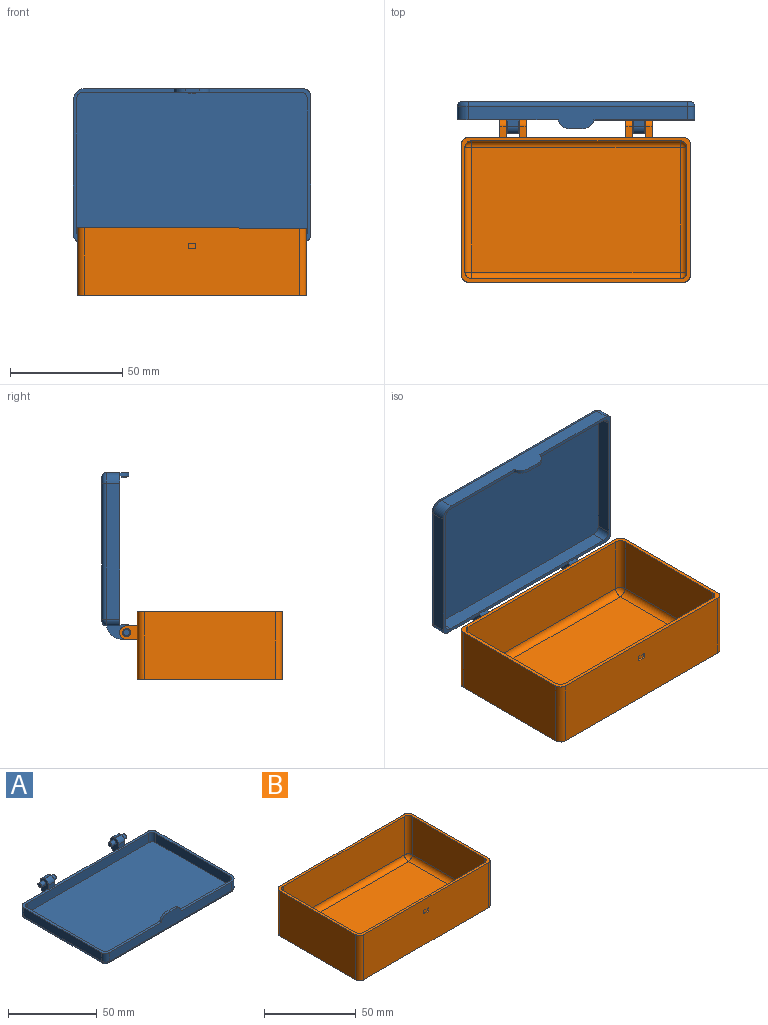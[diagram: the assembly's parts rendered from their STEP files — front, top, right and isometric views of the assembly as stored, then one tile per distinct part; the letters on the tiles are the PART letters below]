
ASSEMBLY  parts=2 mates=1
PART A: 158 faces, bbox 761.3x75.2x14.2 mm
  f0: plane 19.3x6mm, normal (0,1,0), area 115.8mm2, adj f1,f11,f28,f132
  f1: plane 105.8x68.3mm, normal (0,0,1), area 480.9mm2, adj f0,f2,f4,f5,f6,f7,f8,f9
  f2: plane 51.2x6mm, normal (0,1,0), area 307.2mm2, adj f1,f28,f128,f134
  f3: plane 101.8x64.3mm, normal (0,0,-1), area 6346.7mm2, adj f21,f22,f23,f24,f25,f26,f27,f28
  f4: plane 19.3x6mm, normal (0,1,0), area 115.8mm2, adj f1,f5,f28,f126
  f5: cylinder r=3mm len=6mm, axis (0,0,1), area 28.3mm2, adj f1,f4,f6,f27
  f6: plane 62.3x6mm, normal (-1,0,0), area 373.8mm2, adj f1,f5,f7,f25
  f7: cylinder r=3mm len=6mm, axis (0,0,1), area 28.3mm2, adj f1,f6,f8,f23
  f8: plane 97.8x10mm, normal (0,-1,0), area 640.9mm2, adj f1,f7,f9,f21,f150,f151,f152
  f9: cylinder r=5mm len=6mm, axis (0,0,1), area 47.1mm2, adj f1,f8,f10,f22
  f10: plane 60.3x6mm, normal (1,0,0), area 361.8mm2, adj f1,f9,f11,f24
  f11: cylinder r=3mm len=6mm, axis (0,0,1), area 28.3mm2, adj f0,f1,f10,f26
  f12: plane 59.3x6.5mm, normal (-1,0,0), area 385.4mm2, adj f1,f13,f19,f20
  f13: cylinder r=3mm len=6.5mm, axis (0,0,1), area 30.6mm2, adj f1,f12,f14,f20
  f14: plane 96.8x6.5mm, normal (0,-1,0), area 629.2mm2, adj f1,f13,f15,f20
  f15: cylinder r=3mm len=6.5mm, axis (0,0,1), area 30.6mm2, adj f1,f14,f16,f20
  f16: plane 59.3x6.5mm, normal (1,0,0), area 385.4mm2, adj f1,f15,f17,f20
  f17: cylinder r=3mm len=6.5mm, axis (0,0,1), area 30.6mm2, adj f1,f16,f18,f20
  f18: plane 96.8x10.5mm, normal (0,1,0), area 677.3mm2, adj f1,f17,f19,f20,f150,f151,f152,f153
  f19: cylinder r=3mm len=6.5mm, axis (0,0,1), area 30.6mm2, adj f1,f12,f18,f20
  f20: plane 102.8x65.3mm, normal (0,0,1), area 6705.1mm2, adj f12,f13,f14,f15,f16,f17,f18,f19
  f21: cylinder r=2mm len=97.8mm, axis (-1,0,0), area 307.2mm2, adj f3,f8,f22,f23
  f22: torus R=3mm, axis (0,0,1), area 21.1mm2, adj f3,f9,f21,f24
  f23: torus R=1mm, axis (0,0,1), area 11.2mm2, adj f3,f7,f21,f25
  f24: cylinder r=2mm len=60.3mm, axis (0,-1,0), area 189.4mm2, adj f3,f10,f22,f26
  f25: cylinder r=2mm len=62.3mm, axis (0,1,0), area 195.7mm2, adj f3,f6,f23,f27
  f26: torus R=1mm, axis (0,0,1), area 11.2mm2, adj f3,f11,f24,f28
  f27: torus R=1mm, axis (0,0,1), area 11.2mm2, adj f3,f5,f25,f28
  f28: cylinder r=2mm len=99.8mm, axis (1,0,0), area 313.5mm2, adj f0,f2,f3,f4,f26,f27,f148,f149
  f29: plane 2.99x0.5mm, normal (1,0,0), area 1.5mm2, adj f3,f30,f47,f48
  f30: plane 0.88x0.5mm, normal (0,1,0), area 0.4mm2, adj f3,f29,f31,f48
  f31: plane 2.99x1.86mm, normal (-0.85,0.53,0), area 1.8mm2, adj f3,f30,f32,f48
  f32: plane 1.83x0.5mm, normal (0,1,0), area 0.9mm2, adj f3,f31,f33,f48
  f33: extruded ~3.4x2.29mm, area 2mm2, adj f3,f32,f34,f48
  f34: extruded ~1.07x0.84mm, area 0.7mm2, adj f3,f33,f35,f48
  f35: extruded ~1.22x0.5mm, area 0.7mm2, adj f3,f34,f36,f48
  f36: extruded ~1.76x0.76mm, area 1mm2, adj f3,f35,f37,f48
  f37: extruded ~2.35x0.58mm, area 1.2mm2, adj f3,f36,f38,f48
  f38: plane 2.27x0.5mm, normal (0,-1,0), area 1.1mm2, adj f3,f37,f39,f48
  f39: plane 7.79x0.5mm, normal (-1,0,0), area 3.9mm2, adj f3,f38,f47,f48
  f40: plane 0.53x0.5mm, normal (0,-1,0), area 0.3mm2, adj f41,f46,f48,f49
  f41: plane 2.1x0.5mm, normal (1,0,0), area 1.1mm2, adj f40,f42,f48,f49
  f42: plane 0.5x0.5mm, normal (0,1,0), area 0.3mm2, adj f41,f43,f48,f49
  f43: extruded ~1.18x0.5mm, area 0.6mm2, adj f42,f44,f48,f49
  f44: extruded ~0.79x0.5mm, area 0.5mm2, adj f43,f45,f48,f49
  f45: extruded ~0.82x0.5mm, area 0.5mm2, adj f44,f46,f48,f49
  f46: extruded ~1.16x0.5mm, area 0.6mm2, adj f40,f45,f48,f49
  f47: plane 1.65x0.5mm, normal (0,1,0), area 0.8mm2, adj f3,f29,f39,f48
  f48: plane 7.79x6.22mm, normal (0,0,-1), area 29.6mm2, adj f29,f30,f31,f32,f33,f34,f35,f36
  f49: plane 2.1x2.06mm, normal (0,0,-1), area 3.8mm2, adj f40,f41,f42,f43,f44,f45,f46
  f50: extruded ~2.85x0.88mm, area 1.5mm2, adj f51,f61,f62,f125
  f51: plane 2.03x0.5mm, normal (0,-1,0), area 1mm2, adj f50,f52,f62,f125
  f52: extruded ~3.37x1.01mm, area 1.8mm2, adj f51,f61,f62,f125
  f53: plane 1.86x0.56mm, normal (-0.96,0.29,0), area 1mm2, adj f3,f54,f60,f62
  f54: plane 1.78x0.5mm, normal (0,1,0), area 0.9mm2, adj f3,f53,f55,f62
  f55: plane 7.82x2.76mm, normal (0.94,-0.33,0), area 4.1mm2, adj f3,f54,f56,f62
  f56: plane 2.02x0.5mm, normal (0,-1,0), area 1mm2, adj f3,f55,f57,f62
  f57: plane 7.82x2.75mm, normal (-0.94,-0.33,0), area 4.1mm2, adj f3,f56,f58,f62
  f58: plane 1.78x0.5mm, normal (0,1,0), area 0.9mm2, adj f3,f57,f59,f62
  f59: plane 1.86x0.56mm, normal (0.96,0.29,0), area 1mm2, adj f3,f58,f60,f62
  f60: plane 2.84x0.5mm, normal (0,1,0), area 1.4mm2, adj f3,f53,f59,f62
  f61: extruded ~0.52x0.5mm, area 0.3mm2, adj f50,f52,f62,f125
  f62: plane 7.82x7.53mm, normal (0,0,-1), area 27.7mm2, adj f50,f51,f52,f53,f54,f55,f56,f57
  f63: plane 4.49x0.5mm, normal (0,1,0), area 2.2mm2, adj f3,f64,f74,f75
  f64: plane 1.36x0.5mm, normal (1,0,0), area 0.7mm2, adj f3,f63,f65,f75
  f65: plane 2.83x0.5mm, normal (0,-1,0), area 1.4mm2, adj f3,f64,f66,f75
  f66: plane 2.01x0.5mm, normal (1,0,0), area 1mm2, adj f3,f65,f67,f75
  f67: plane 2.64x0.5mm, normal (0,1,0), area 1.3mm2, adj f3,f66,f68,f75
  f68: plane 1.35x0.5mm, normal (1,0,0), area 0.7mm2, adj f3,f67,f69,f75
  f69: plane 2.64x0.5mm, normal (0,-1,0), area 1.3mm2, adj f3,f68,f70,f75
  f70: plane 1.71x0.5mm, normal (1,0,0), area 0.9mm2, adj f3,f69,f71,f75
  f71: plane 2.83x0.5mm, normal (0,1,0), area 1.4mm2, adj f3,f70,f72,f75
  f72: plane 1.35x0.5mm, normal (1,0,0), area 0.7mm2, adj f3,f71,f73,f75
  f73: plane 4.49x0.5mm, normal (0,-1,0), area 2.2mm2, adj f3,f72,f74,f75
  f74: plane 7.79x0.5mm, normal (-1,0,0), area 3.9mm2, adj f3,f63,f73,f75
  f75: plane 7.79x4.49mm, normal (0,0,-1), area 24.1mm2, adj f63,f64,f65,f66,f67,f68,f69,f70
  f76: plane 2.1x0.5mm, normal (0,1,0), area 1mm2, adj f3,f77,f89,f90
  f77: plane 7.79x0.5mm, normal (1,0,0), area 3.9mm2, adj f3,f76,f78,f90
  f78: plane 1.49x0.5mm, normal (0,-1,0), area 0.7mm2, adj f3,f77,f79,f90
  f79: plane 3.69x0.5mm, normal (-1,0,0), area 1.8mm2, adj f3,f78,f80,f90
  f80: extruded ~2.15x0.5mm, area 1.1mm2, adj f3,f79,f81,f90
  f81: plane 0.5x0.04mm, normal (0,-1,0), area 0mm2, adj f3,f80,f82,f90
  f82: plane 5.84x3.38mm, normal (0.87,-0.5,0), area 3.4mm2, adj f3,f81,f83,f90
  f83: plane 2.08x0.5mm, normal (0,-1,0), area 1mm2, adj f3,f82,f84,f90
  f84: plane 7.79x0.5mm, normal (-1,0,0), area 3.9mm2, adj f3,f83,f85,f90
  f85: plane 1.48x0.5mm, normal (0,1,0), area 0.7mm2, adj f3,f84,f86,f90
  f86: plane 3.67x0.5mm, normal (1,0,0), area 1.8mm2, adj f3,f85,f87,f90
  f87: extruded ~2.23x0.5mm, area 1.1mm2, adj f3,f86,f88,f90
  f88: plane 0.5x0.05mm, normal (0,1,0), area 0mm2, adj f3,f87,f89,f90
  f89: plane 5.89x3.39mm, normal (-0.87,0.5,0), area 3.4mm2, adj f3,f76,f88,f90
  f90: plane 7.79x6.91mm, normal (0,0,-1), area 34.4mm2, adj f76,f77,f78,f79,f80,f81,f82,f83
  f91: plane 7.79x0.5mm, normal (-1,0,0), area 3.9mm2, adj f3,f92,f94,f95
  f92: plane 1.65x0.5mm, normal (0,1,0), area 0.8mm2, adj f3,f91,f93,f95
  f93: plane 7.79x0.5mm, normal (1,0,0), area 3.9mm2, adj f3,f92,f94,f95
  f94: plane 1.65x0.5mm, normal (0,-1,0), area 0.8mm2, adj f3,f91,f93,f95
  f95: plane 7.79x1.65mm, normal (0,0,-1), area 12.9mm2, adj f91,f92,f93,f94
  f96: plane 1.65x0.5mm, normal (0,1,0), area 0.8mm2, adj f3,f97,f103,f104
  f97: plane 6.42x0.5mm, normal (1,0,0), area 3.2mm2, adj f3,f96,f98,f104
  f98: plane 2.11x0.5mm, normal (0,1,0), area 1.1mm2, adj f3,f97,f99,f104
  f99: plane 1.37x0.5mm, normal (1,0,0), area 0.7mm2, adj f3,f98,f100,f104
  f100: plane 5.88x0.5mm, normal (0,-1,0), area 2.9mm2, adj f3,f99,f101,f104
  f101: plane 1.37x0.5mm, normal (-1,0,0), area 0.7mm2, adj f3,f100,f102,f104
  f102: plane 2.12x0.5mm, normal (0,1,0), area 1.1mm2, adj f3,f101,f103,f104
  f103: plane 6.42x0.5mm, normal (-1,0,0), area 3.2mm2, adj f3,f96,f102,f104
  f104: plane 7.79x5.88mm, normal (0,0,-1), area 18.7mm2, adj f96,f97,f98,f99,f100,f101,f102,f103
  f105: plane 6.11x1.88mm, normal (-0.96,0.29,0), area 3.2mm2, adj f3,f106,f123,f124
  f106: plane 1.51x0.5mm, normal (0,1,0), area 0.8mm2, adj f3,f105,f107,f124
  f107: plane 6.1x2.01mm, normal (0.95,0.31,0), area 3.2mm2, adj f3,f106,f108,f124
  f108: plane 0.5x0.05mm, normal (0,1,0), area 0mm2, adj f3,f107,f109,f124
  f109: extruded ~1.81x0.5mm, area 0.9mm2, adj f3,f108,f110,f124
  f110: extruded ~0.6x0.5mm, area 0.3mm2, adj f3,f109,f111,f124
  f111: plane 3.69x0.5mm, normal (-1,0,0), area 1.8mm2, adj f3,f110,f112,f124
  f112: plane 1.54x0.5mm, normal (0,1,0), area 0.8mm2, adj f3,f111,f113,f124
  f113: plane 7.79x0.5mm, normal (1,0,0), area 3.9mm2, adj f3,f112,f114,f124
  f114: plane 2.25x0.5mm, normal (0,-1,0), area 1.1mm2, adj f3,f113,f115,f124
  f115: plane 5.96x1.96mm, normal (-0.95,-0.31,0), area 3.1mm2, adj f3,f114,f116,f124
  f116: plane 0.5x0.03mm, normal (0,-1,0), area 0mm2, adj f3,f115,f117,f124
  f117: plane 5.96x1.84mm, normal (0.96,-0.3,0), area 3.1mm2, adj f3,f116,f118,f124
  f118: plane 2.25x0.5mm, normal (0,-1,0), area 1.1mm2, adj f3,f117,f119,f124
  f119: plane 7.79x0.5mm, normal (-1,0,0), area 3.9mm2, adj f3,f118,f120,f124
  f120: plane 1.48x0.5mm, normal (0,1,0), area 0.7mm2, adj f3,f119,f121,f124
  f121: plane 3.62x0.5mm, normal (1,0,0), area 1.8mm2, adj f3,f120,f122,f124
  f122: extruded ~2.49x0.5mm, area 1.2mm2, adj f3,f121,f123,f124
  f123: plane 0.5x0.05mm, normal (0,1,0), area 0mm2, adj f3,f105,f122,f124
  f124: plane 8.33x7.79mm, normal (0,0,-1), area 41.9mm2, adj f105,f106,f107,f108,f109,f110,f111,f112
  f125: plane 3.37x2.03mm, normal (0,0,-1), area 3.4mm2, adj f50,f51,f52,f61
  f126: plane 12.18x6.68mm, normal (-1,0,0), area 54.9mm2, adj f1,f4,f127,f129,f130,f138,f139,f140
  f127: plane 5x3mm, normal (0,-1,0), area 15mm2, adj f1,f126,f128,f139
  f128: plane 12.18x6.67mm, normal (1,0,0), area 54.8mm2, adj f1,f2,f127,f129,f130,f138,f139,f142
  f129: plane 5x2.07mm, normal (0,1,0), area 10.4mm2, adj f126,f128,f138,f149
  f130: plane 5x0.5mm, normal (0,0,1), area 2.5mm2, adj f126,f128,f138,f139
  f131: plane 5x3mm, normal (0,-1,0), area 15mm2, adj f1,f132,f134,f137
  f132: plane 12x6.5mm, normal (1,0,0), area 54.9mm2, adj f0,f1,f131,f133,f135,f136,f137,f144
  f133: plane 5x2.07mm, normal (0,1,0), area 10.4mm2, adj f132,f134,f136,f148
  f134: plane 12x6.5mm, normal (-1,0,0), area 54.9mm2, adj f1,f2,f131,f133,f135,f136,f137,f146
  f135: plane 5x0.5mm, normal (0,0,1), area 2.5mm2, adj f132,f134,f136,f137
  f136: cylinder r=3mm len=5mm, axis (1,0,0), area 23.6mm2, adj f132,f133,f134,f135
  f137: cylinder r=3mm len=5mm, axis (-1,0,0), area 23.6mm2, adj f131,f132,f134,f135
  f138: cylinder r=3mm len=5.01mm, axis (1,0,0), area 23.6mm2, adj f126,f128,f129,f130
  f139: cylinder r=3mm len=5mm, axis (-1,0,0), area 23.6mm2, adj f126,f127,f128,f130
  f140: cylinder r=1.4mm len=3.4mm, axis (1,0,0), area 29.9mm2, adj f126,f141
  f141: plane 2.8x2.8mm, normal (-1,0,0), area 6.2mm2, adj f140
  f142: cylinder r=1.4mm len=3.4mm, axis (-1,0,0), area 29.9mm2, adj f128,f143
  f143: plane 2.8x2.8mm, normal (1,0,0), area 6.2mm2, adj f142
  f144: cylinder r=1.4mm len=3.4mm, axis (-1,0,0), area 29.9mm2, adj f132,f145
  f145: plane 2.8x2.8mm, normal (1,0,0), area 6.2mm2, adj f144
  f146: cylinder r=1.4mm len=3.4mm, axis (1,0,0), area 29.9mm2, adj f134,f147
  f147: plane 2.8x2.8mm, normal (-1,0,0), area 6.2mm2, adj f146
  f148: cylinder r=7mm len=6.93mm, axis (1,0,0), area 50mm2, adj f28,f132,f133,f134
  f149: bspline ~761.14x6.97mm, area 50mm2, adj f28,f126,f128,f129
  f150: plane 6.2x1.5mm, normal (0,0,1), area 9.3mm2, adj f8,f18,f151,f152
  f151: cylinder r=5mm len=4.9mm, axis (0,1,0), area 10.3mm2, adj f1,f8,f18,f150
  f152: cylinder r=5mm len=4.9mm, axis (0,1,0), area 10.3mm2, adj f1,f8,f18,f150
  f153: plane 2x0.8mm, normal (-1,0,0), area 1.6mm2, adj f18,f154,f156,f157
  f154: plane 3x0.8mm, normal (0,0,1), area 2.4mm2, adj f18,f153,f155,f157
  f155: plane 2x0.8mm, normal (1,0,0), area 1.6mm2, adj f18,f154,f156,f157
  f156: plane 3x0.8mm, normal (0,0,-1), area 2.4mm2, adj f18,f153,f155,f157
  f157: plane 3x2mm, normal (0,1,0), area 6mm2, adj f153,f154,f155,f156
PART B: 56 faces, bbox 102x72.5x30 mm
  f0: plane 96x30mm, normal (0,-1,0), area 2871.8mm2, adj f2,f5,f6,f9,f39,f40,f41,f42
  f1: plane 96x30mm, normal (0,1,0), area 2808mm2, adj f2,f3,f8,f9,f15,f16,f17,f18
  f2: plane 102x64.5mm, normal (0,0,1), area 490.5mm2, adj f0,f1,f3,f4,f5,f6,f7,f8
  f3: cylinder r=3mm len=30mm, axis (0,0,1), area 141.4mm2, adj f1,f2,f4,f9
  f4: plane 58.5x30mm, normal (-1,0,0), area 1755mm2, adj f2,f3,f5,f9
  f5: cylinder r=3mm len=30mm, axis (0,0,1), area 141.4mm2, adj f0,f2,f4,f9
  f6: cylinder r=3mm len=30mm, axis (0,0,1), area 141.4mm2, adj f0,f2,f7,f9
  f7: plane 58.5x30mm, normal (1,0,0), area 1755mm2, adj f2,f6,f8,f9
  f8: cylinder r=3mm len=30mm, axis (0,0,1), area 141.4mm2, adj f1,f2,f7,f9
  f9: plane 102x64.5mm, normal (0,0,-1), area 6571.3mm2, adj f0,f1,f3,f4,f5,f6,f7,f8
  f10: plane 93x25.5mm, normal (0,1,0), area 2371.5mm2, adj f2,f49,f52,f55
  f11: plane 93x55.5mm, normal (0,0,1), area 5161.5mm2, adj f45,f50,f51,f55
  f12: plane 93x25.5mm, normal (0,-1,0), area 2371.5mm2, adj f2,f44,f45,f46
  f13: plane 55.5x25.5mm, normal (1,0,0), area 1415.3mm2, adj f2,f44,f49,f50
  f14: plane 55.5x25.5mm, normal (-1,0,0), area 1415.3mm2, adj f2,f46,f51,f52
  f15: plane 8x6mm, normal (-1,0,0), area 34mm2, adj f1,f17,f18,f34,f38
  f16: plane 8x6mm, normal (1,0,0), area 34mm2, adj f1,f17,f18,f34,f38
  f17: plane 5x3mm, normal (0,0,-1), area 15mm2, adj f1,f15,f16,f38
  f18: plane 5x3mm, normal (0,0,1), area 15mm2, adj f1,f15,f16,f38
  f19: plane 8x6mm, normal (-1,0,0), area 34mm2, adj f1,f21,f22,f33,f37
  f20: plane 8x6mm, normal (1,0,0), area 34mm2, adj f1,f21,f22,f33,f37
  f21: plane 5x3mm, normal (0,0,-1), area 15mm2, adj f1,f19,f20,f37
  f22: plane 5x3mm, normal (0,0,1), area 15mm2, adj f1,f19,f20,f37
  f23: plane 8x6mm, normal (-1,0,0), area 34mm2, adj f1,f25,f26,f32,f36
  f24: plane 8x6mm, normal (1,0,0), area 34mm2, adj f1,f25,f26,f32,f36
  f25: plane 5x3mm, normal (0,0,-1), area 15mm2, adj f1,f23,f24,f36
  f26: plane 5x3mm, normal (0,0,1), area 15mm2, adj f1,f23,f24,f36
  f27: plane 8x6mm, normal (-1,0,0), area 34mm2, adj f1,f29,f30,f31,f35
  f28: plane 8x6mm, normal (1,0,0), area 34mm2, adj f1,f29,f30,f31,f35
  f29: plane 5x3mm, normal (0,0,-1), area 15mm2, adj f1,f27,f28,f35
  f30: plane 5x3mm, normal (0,0,1), area 15mm2, adj f1,f27,f28,f35
  f31: cylinder r=1.8mm len=3.6mm, axis (1,0,0), area 33.9mm2, adj f27,f28
  f32: cylinder r=1.8mm len=3.6mm, axis (1,0,0), area 33.9mm2, adj f23,f24
  f33: cylinder r=1.8mm len=3.6mm, axis (1,0,0), area 33.9mm2, adj f19,f20
  f34: cylinder r=1.8mm len=3.6mm, axis (1,0,0), area 33.9mm2, adj f15,f16
  f35: cylinder r=3mm len=6mm, axis (1,0,0), area 28.3mm2, adj f27,f28,f29,f30
  f36: cylinder r=3mm len=6mm, axis (1,0,0), area 28.3mm2, adj f23,f24,f25,f26
  f37: cylinder r=3mm len=6mm, axis (1,0,0), area 28.3mm2, adj f19,f20,f21,f22
  f38: cylinder r=3mm len=6mm, axis (1,0,0), area 28.3mm2, adj f15,f16,f17,f18
  f39: plane 3.4x0.75mm, normal (0,0,1), area 2.6mm2, adj f0,f40,f42,f43
  f40: plane 2.4x0.75mm, normal (-1,0,0), area 1.8mm2, adj f0,f39,f41,f43
  f41: plane 3.4x0.75mm, normal (0,0,-1), area 2.6mm2, adj f0,f40,f42,f43
  f42: plane 2.4x0.75mm, normal (1,0,0), area 1.8mm2, adj f0,f39,f41,f43
  f43: plane 3.4x2.4mm, normal (0,-1,0), area 8.2mm2, adj f39,f40,f41,f42
  f44: cylinder r=3mm len=25.5mm, axis (0,0,1), area 120.2mm2, adj f2,f12,f13,f47
  f45: cylinder r=3mm len=93mm, axis (1,0,0), area 438.3mm2, adj f11,f12,f47,f48
  f46: cylinder r=3mm len=25.5mm, axis (0,0,-1), area 120.2mm2, adj f2,f12,f14,f48
  f47: sphere r=3mm, area 14.1mm2, adj f44,f45,f50
  f48: sphere r=3mm, area 14.1mm2, adj f45,f46,f51
  f49: cylinder r=3mm len=25.5mm, axis (0,0,-1), area 120.2mm2, adj f2,f10,f13,f53
  f50: cylinder r=3mm len=55.5mm, axis (0,1,0), area 261.5mm2, adj f11,f13,f47,f53
  f51: cylinder r=3mm len=55.5mm, axis (0,-1,0), area 261.5mm2, adj f11,f14,f48,f54
  f52: cylinder r=3mm len=25.5mm, axis (0,0,1), area 120.2mm2, adj f2,f10,f14,f54
  f53: sphere r=3mm, area 14.1mm2, adj f49,f50,f55
  f54: sphere r=3mm, area 14.1mm2, adj f51,f52,f55
  f55: cylinder r=3mm len=93mm, axis (-1,0,0), area 438.3mm2, adj f10,f11,f53,f54
PLACE A rot(axis=(0,-0.71,0.71),180deg) t=(-45.47,-104.12,-71.42)mm
PLACE B rot(axis=(-0.18,0.89,-0.42),0deg) t=(-45.5,-144.18,-99.36)mm
MATE revolute A.f136 <-> B.f31  axis (1,0,0) through (-11.5,-107.15,-108.59)mm
